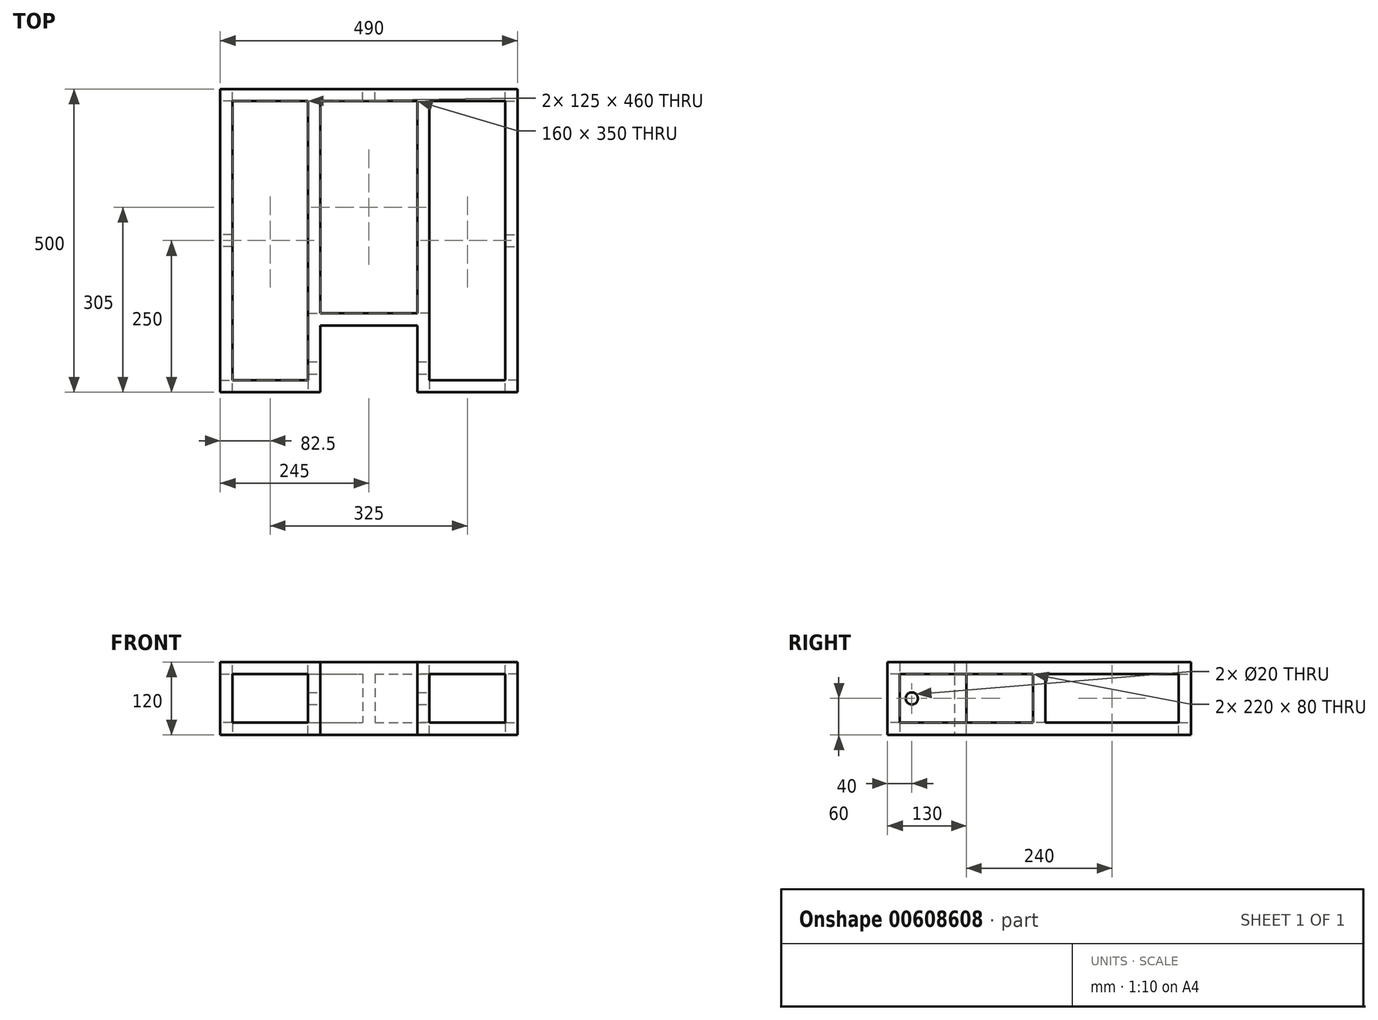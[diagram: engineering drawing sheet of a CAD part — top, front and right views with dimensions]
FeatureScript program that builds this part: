
annotation { "Feature Type Name" : "Feature", "Feature Type Description" : "" }
export const myFeature = defineFeature(function(context is Context, id is Id, definition is map)
    precondition{}
    {
        {
            var Q0;
            Q0=qCreatedBy(makeId("Front.planeOp"),FACE);
            var sketch = newSketch(context, id + "F0", { "sketchPlane" : qUnion([Q0])});
            skLineSegment(sketch, "E0.bottom", {"start": v(0, 0) * mm, "end": v(20, 0) * mm});
            skLineSegment(sketch, "E0.top", {"start": v(0, 20) * mm, "end": v(20, 20) * mm});
            skLineSegment(sketch, "E0.left", {"start": v(0, 0) * mm, "end": v(0, 20) * mm});
            skLineSegment(sketch, "E0.right", {"start": v(20, 0) * mm, "end": v(20, 20) * mm});
            skSolve(sketch);
        }
        {
            var Q0;
            Q0=makeQuery(id+"F0.imprint","IMPRINT",FACE,{"disambiguationData":[TD([[makeQuery(id+"F0.imprint","IMPRINT",EDGE,{"derivedFrom":sQuery(id+"F0.wireOp",EDGE,"E0.bottom")}),1.0]])]});
            extrude(context, id + "F1", {"entities" : qUnion([Q0]), "depth" : 500 * mm, "offsetDistance" : 25 * mm});
        }
        {
            var Q0;
            Q0=makeQuery(id+"F1.opExtrude","SWEPT_FACE",FACE,{"disambiguationData":[OSD([sQuery(id+"F0.wireOp",EDGE,"E0.left")])]});
            var sketch = newSketch(context, id + "F2", { "sketchPlane" : qUnion([Q0])});
            skLineSegment(sketch, "E1.bottom", {"start": v(0, 20) * mm, "end": v(20, 20) * mm});
            skLineSegment(sketch, "E1.top", {"start": v(0, 0) * mm, "end": v(20, 0) * mm});
            skLineSegment(sketch, "E1.left", {"start": v(0, 20) * mm, "end": v(0, 0) * mm});
            skLineSegment(sketch, "E1.right", {"start": v(20, 20) * mm, "end": v(20, 0) * mm});
            skLineSegment(sketch, "E2.bottom", {"start": v(500, 0) * mm, "end": v(480, 0) * mm});
            skLineSegment(sketch, "E2.top", {"start": v(500, 20) * mm, "end": v(480, 20) * mm});
            skLineSegment(sketch, "E2.left", {"start": v(500, 0) * mm, "end": v(500, 20) * mm});
            skLineSegment(sketch, "E2.right", {"start": v(480, 0) * mm, "end": v(480, 20) * mm});
            skSolve(sketch);
        }
        {
            var Q0;
            Q0 = qSketchRegion(id + "F2", true);
            extrude(context, id + "F3", {"entities" : qUnion([Q0]), "operationType" : NewBodyOperationType.ADD, "depth" : 470 * mm, "offsetDistance" : 25 * mm});
        }
        {
            var Q0;
            Q0=makeQuery(id+"F3.opExtrude","SWEPT_FACE",FACE,{"disambiguationData":[OSD([sQuery(id+"F2.wireOp",EDGE,"E1.right")])]});
            var sketch = newSketch(context, id + "F4", { "sketchPlane" : qUnion([Q0])});
            skLineSegment(sketch, "E3.bottom", {"start": v(-470, 20) * mm, "end": v(-450, 20) * mm});
            skLineSegment(sketch, "E3.top", {"start": v(-470, 0) * mm, "end": v(-450, 0) * mm});
            skLineSegment(sketch, "E3.left", {"start": v(-470, 20) * mm, "end": v(-470, 0) * mm});
            skLineSegment(sketch, "E3.right", {"start": v(-450, 20) * mm, "end": v(-450, 0) * mm});
            skSolve(sketch);
        }
        {
            var Q0;
            Q0=makeQuery(id+"F4.imprint","IMPRINT",FACE,{"disambiguationData":[TD([[makeQuery(id+"F4.imprint","IMPRINT",EDGE,{"derivedFrom":sQuery(id+"F4.wireOp",EDGE,"E3.bottom")}),-1.0]])]});
            extrude(context, id + "F5", {"entities" : qUnion([Q0]), "operationType" : NewBodyOperationType.ADD, "endBound" : BoundingType.UP_TO_NEXT, "depth" : 25 * mm, "offsetDistance" : 25 * mm});
        }
        {
            var Q0;
            Q0=makeQuery(id+"F3.opExtrude","SWEPT_FACE",FACE,{"disambiguationData":[OSD([sQuery(id+"F2.wireOp",EDGE,"E2.right")])]});
            var sketch = newSketch(context, id + "F6", { "sketchPlane" : qUnion([Q0])});
            skLineSegment(sketch, "E4.bottom", {"start": v(125, 20) * mm, "end": v(145, 20) * mm});
            skLineSegment(sketch, "E4.top", {"start": v(125, 0) * mm, "end": v(145, 0) * mm});
            skLineSegment(sketch, "E4.left", {"start": v(125, 20) * mm, "end": v(125, 0) * mm});
            skLineSegment(sketch, "E4.right", {"start": v(145, 20) * mm, "end": v(145, 0) * mm});
            skLineSegment(sketch, "E5.bottom", {"start": v(305, 20) * mm, "end": v(325, 20) * mm});
            skLineSegment(sketch, "E5.top", {"start": v(305, 0) * mm, "end": v(325, 0) * mm});
            skLineSegment(sketch, "E5.left", {"start": v(305, 20) * mm, "end": v(305, 0) * mm});
            skLineSegment(sketch, "E5.right", {"start": v(325, 20) * mm, "end": v(325, 0) * mm});
            skSolve(sketch);
        }
        {
            var Q0;
            Q0=makeQuery(id+"F6.imprint","IMPRINT",FACE,{"disambiguationData":[TD([[makeQuery(id+"F6.imprint","IMPRINT",EDGE,{"derivedFrom":sQuery(id+"F6.wireOp",EDGE,"E4.bottom")}),1.0]])]});
            var Q1;
            Q1=makeQuery(id+"F6.imprint","IMPRINT",FACE,{"disambiguationData":[TD([[makeQuery(id+"F6.imprint","IMPRINT",EDGE,{"derivedFrom":sQuery(id+"F6.wireOp",EDGE,"E5.bottom")}),1.0]])]});
            extrude(context, id + "F7", {"entities" : qUnion([Q0, Q1]), "operationType" : NewBodyOperationType.ADD, "depth" : 110 * mm, "offsetDistance" : 25 * mm});
        }
        {
            var Q0;
            Q0=makeQuery(id+"F7.opExtrude","SWEPT_FACE",FACE,{"disambiguationData":[OSD([sQuery(id+"F6.wireOp",EDGE,"E4.right")])]});
            var sketch = newSketch(context, id + "F8", { "sketchPlane" : qUnion([Q0])});
            skLineSegment(sketch, "E6.bottom", {"start": v(370, 20) * mm, "end": v(390, 20) * mm});
            skLineSegment(sketch, "E6.top", {"start": v(370, 0) * mm, "end": v(390, 0) * mm});
            skLineSegment(sketch, "E6.left", {"start": v(370, 20) * mm, "end": v(370, 0) * mm});
            skLineSegment(sketch, "E6.right", {"start": v(390, 20) * mm, "end": v(390, 0) * mm});
            skSolve(sketch);
        }
        {
            var Q0;
            Q0=makeQuery(id+"F8.imprint","IMPRINT",FACE,{"disambiguationData":[TD([[makeQuery(id+"F8.imprint","IMPRINT",EDGE,{"derivedFrom":sQuery(id+"F8.wireOp",EDGE,"E6.bottom")}),-1.0]])]});
            extrude(context, id + "F9", {"entities" : qUnion([Q0]), "operationType" : NewBodyOperationType.ADD, "endBound" : BoundingType.UP_TO_NEXT, "depth" : 25 * mm, "offsetDistance" : 25 * mm});
        }
        {
            var Q0;
            Q0=makeQuery(id+"F5.boolean.opBoolean","MERGE",FACE,{"derivedFrom":[makeQuery(id+"F3.boolean.opBoolean","MERGE",FACE,{"derivedFrom":[makeQuery(id+"F1.opExtrude","SWEPT_FACE",FACE,{"disambiguationData":[OSD([sQuery(id+"F0.wireOp",EDGE,"E0.top")])]}),makeQuery(id+"F3.opExtrude","SWEPT_FACE",FACE,{"disambiguationData":[OSD([sQuery(id+"F2.wireOp",EDGE,"E1.bottom")])]}),makeQuery(id+"F3.opExtrude","SWEPT_FACE",FACE,{"disambiguationData":[OSD([sQuery(id+"F2.wireOp",EDGE,"E2.top")])]})]}),makeQuery(id+"F5.opExtrude","SWEPT_FACE",FACE,{"disambiguationData":[OSD([sQuery(id+"F4.wireOp",EDGE,"E3.bottom")])]})]});
            var sketch = newSketch(context, id + "F10", { "sketchPlane" : qUnion([Q0])});
            skLineSegment(sketch, "E7.bottom", {"start": v(-470, -500) * mm, "end": v(-450, -500) * mm});
            skLineSegment(sketch, "E7.top", {"start": v(-470, -480) * mm, "end": v(-450, -480) * mm});
            skLineSegment(sketch, "E7.left", {"start": v(-470, -500) * mm, "end": v(-470, -480) * mm});
            skLineSegment(sketch, "E7.right", {"start": v(-450, -500) * mm, "end": v(-450, -480) * mm});
            skLineSegment(sketch, "E8.bottom", {"start": v(20, -500) * mm, "end": v(0, -500) * mm});
            skLineSegment(sketch, "E8.top", {"start": v(20, -480) * mm, "end": v(0, -480) * mm});
            skLineSegment(sketch, "E8.left", {"start": v(20, -500) * mm, "end": v(20, -480) * mm});
            skLineSegment(sketch, "E8.right", {"start": v(0, -500) * mm, "end": v(0, -480) * mm});
            skLineSegment(sketch, "E9.bottom", {"start": v(-450, -20) * mm, "end": v(-470, -20) * mm});
            skLineSegment(sketch, "E9.top", {"start": v(-450, 0) * mm, "end": v(-470, 0) * mm});
            skLineSegment(sketch, "E9.left", {"start": v(-450, -20) * mm, "end": v(-450, 0) * mm});
            skLineSegment(sketch, "E9.right", {"start": v(-470, -20) * mm, "end": v(-470, 0) * mm});
            skLineSegment(sketch, "E10.bottom", {"start": v(0, -20) * mm, "end": v(20, -20) * mm});
            skLineSegment(sketch, "E10.top", {"start": v(0, 0) * mm, "end": v(20, 0) * mm});
            skLineSegment(sketch, "E10.left", {"start": v(0, -20) * mm, "end": v(0, 0) * mm});
            skLineSegment(sketch, "E10.right", {"start": v(20, -20) * mm, "end": v(20, 0) * mm});
            skLineSegment(sketch, "E11.bottom", {"start": v(0, -260) * mm, "end": v(20, -260) * mm});
            skLineSegment(sketch, "E11.top", {"start": v(0, -240) * mm, "end": v(20, -240) * mm});
            skLineSegment(sketch, "E11.left", {"start": v(0, -260) * mm, "end": v(0, -240) * mm});
            skLineSegment(sketch, "E11.right", {"start": v(20, -260) * mm, "end": v(20, -240) * mm});
            skLineSegment(sketch, "E12.bottom", {"start": v(-450, -260) * mm, "end": v(-470, -260) * mm});
            skLineSegment(sketch, "E12.top", {"start": v(-450, -240) * mm, "end": v(-470, -240) * mm});
            skLineSegment(sketch, "E12.left", {"start": v(-450, -260) * mm, "end": v(-450, -240) * mm});
            skLineSegment(sketch, "E12.right", {"start": v(-470, -260) * mm, "end": v(-470, -240) * mm});
            skLineSegment(sketch, "E13.bottom", {"start": v(-325, -370) * mm, "end": v(-305, -370) * mm});
            skLineSegment(sketch, "E13.top", {"start": v(-325, -500) * mm, "end": v(-305, -500) * mm});
            skLineSegment(sketch, "E13.left", {"start": v(-325, -370) * mm, "end": v(-325, -500) * mm});
            skLineSegment(sketch, "E13.right", {"start": v(-305, -370) * mm, "end": v(-305, -500) * mm});
            skLineSegment(sketch, "E14.bottom", {"start": v(-125, -370) * mm, "end": v(-145, -370) * mm});
            skLineSegment(sketch, "E14.top", {"start": v(-125, -500) * mm, "end": v(-145, -500) * mm});
            skLineSegment(sketch, "E14.left", {"start": v(-125, -370) * mm, "end": v(-125, -500) * mm});
            skLineSegment(sketch, "E14.right", {"start": v(-145, -370) * mm, "end": v(-145, -500) * mm});
            skLineSegment(sketch, "E15.bottom", {"start": v(-235, -20) * mm, "end": v(-215, -20) * mm});
            skLineSegment(sketch, "E15.top", {"start": v(-235, 0) * mm, "end": v(-215, 0) * mm});
            skLineSegment(sketch, "E15.left", {"start": v(-235, -20) * mm, "end": v(-235, 0) * mm});
            skLineSegment(sketch, "E15.right", {"start": v(-215, -20) * mm, "end": v(-215, 0) * mm});
            skSolve(sketch);
        }
        {
            var Q0;
            Q0 = qSketchRegion(id + "F10", true);
            extrude(context, id + "F11", {"entities" : qUnion([Q0]), "operationType" : NewBodyOperationType.ADD, "depth" : 40 * mm, "offsetDistance" : 25 * mm});
        }
        {
            var Q0;
            Q0=makeQuery(id+"F1.opExtrude","SWEPT_BODY",BODY,{"disambiguationData":[OSD([sQuery(id+"F0.wireOp",EDGE,"E0.bottom"),sQuery(id+"F0.wireOp",EDGE,"E0.top"),sQuery(id+"F0.wireOp",EDGE,"E0.left"),sQuery(id+"F0.wireOp",EDGE,"E0.right")])]});
            var Q1;
            Q1=makeQuery(id+"F11.opExtrude","CAP_FACE",FACE,{"disambiguationData":[OSD([sQuery(id+"F10.wireOp",EDGE,"E10.bottom"),sQuery(id+"F10.wireOp",EDGE,"E10.top"),sQuery(id+"F10.wireOp",EDGE,"E10.left"),sQuery(id+"F10.wireOp",EDGE,"E10.right")])],"isStart":false});
            mirror(context, id + "F12", {"operationType" : NewBodyOperationType.ADD, "entities" : qUnion([Q0]), "mirrorPlane" : qUnion([Q1])});
        }
        {
            var Q0;
            Q0=makeQuery(id+"F12.opPattern","COPY",FACE,{"derivedFrom":makeQuery(id+"F9.boolean.opBoolean","MERGE",FACE,{"derivedFrom":[makeQuery(id+"F7.boolean.opBoolean","MERGE",FACE,{"derivedFrom":[makeQuery(id+"F5.boolean.opBoolean","MERGE",FACE,{"derivedFrom":[makeQuery(id+"F3.boolean.opBoolean","MERGE",FACE,{"derivedFrom":[makeQuery(id+"F1.opExtrude","SWEPT_FACE",FACE,{"disambiguationData":[OSD([sQuery(id+"F0.wireOp",EDGE,"E0.bottom")])]}),makeQuery(id+"F3.opExtrude","SWEPT_FACE",FACE,{"disambiguationData":[OSD([sQuery(id+"F2.wireOp",EDGE,"E1.top")])]}),makeQuery(id+"F3.opExtrude","SWEPT_FACE",FACE,{"disambiguationData":[OSD([sQuery(id+"F2.wireOp",EDGE,"E2.bottom")])]})]}),makeQuery(id+"F5.opExtrude","SWEPT_FACE",FACE,{"disambiguationData":[OSD([sQuery(id+"F4.wireOp",EDGE,"E3.top")])]})]}),makeQuery(id+"F7.opExtrude","SWEPT_FACE",FACE,{"disambiguationData":[OSD([sQuery(id+"F6.wireOp",EDGE,"E4.top")])]}),makeQuery(id+"F7.opExtrude","SWEPT_FACE",FACE,{"disambiguationData":[OSD([sQuery(id+"F6.wireOp",EDGE,"E5.top")])]})]}),makeQuery(id+"F9.opExtrude","SWEPT_FACE",FACE,{"disambiguationData":[OSD([sQuery(id+"F8.wireOp",EDGE,"E6.top")])]})]}),"instanceName":"1"});
            var sketch = newSketch(context, id + "F13", { "sketchPlane" : qUnion([Q0])});
            skLineSegment(sketch, "E16.bottom", {"start": v(-305, -480) * mm, "end": v(-145, -480) * mm});
            skLineSegment(sketch, "E16.top", {"start": v(-305, -500) * mm, "end": v(-145, -500) * mm});
            skLineSegment(sketch, "E16.left", {"start": v(-305, -480) * mm, "end": v(-305, -500) * mm});
            skLineSegment(sketch, "E16.right", {"start": v(-145, -480) * mm, "end": v(-145, -500) * mm});
            skSolve(sketch);
        }
        {
            var Q0;
            Q0 = qSketchRegion(id + "F13", true);
            extrude(context, id + "F14", {"entities" : qUnion([Q0]), "operationType" : NewBodyOperationType.REMOVE, "endBound" : BoundingType.THROUGH_ALL, "oppositeDirection" : true, "depth" : 25 * mm, "offsetDistance" : 25 * mm});
        }
        {
            var Q0;
            {var subQ0=makeQuery(id+"F11.boolean.opBoolean","MERGE",FACE,{"derivedFrom":[makeQuery(id+"F7.opExtrude","SWEPT_FACE",FACE,{"disambiguationData":[OSD([sQuery(id+"F6.wireOp",EDGE,"E4.left")])]}),makeQuery(id+"F11.opExtrude","SWEPT_FACE",FACE,{"disambiguationData":[OSD([sQuery(id+"F10.wireOp",EDGE,"E14.left")])]})]});Q0=makeQuery(id+"F12.boolean.opBoolean","MERGE",FACE,{"derivedFrom":[subQ0,makeQuery(id+"F12.opPattern","COPY",FACE,{"derivedFrom":subQ0,"instanceName":"1"})]});}
            var sketch = newSketch(context, id + "F15", { "sketchPlane" : qUnion([Q0])});
            skPoint(sketch, "E17", {"position": v(-460, 60) * mm});
            skSolve(sketch);
        }
        {
            var Q0;
            Q0=sQuery(id+"F15.wireOp",VERTEX,"E17");
            var Q1;
            Q1=makeQuery(id+"F1.opExtrude","SWEPT_BODY",BODY,{"disambiguationData":[OSD([sQuery(id+"F0.wireOp",EDGE,"E0.bottom"),sQuery(id+"F0.wireOp",EDGE,"E0.top"),sQuery(id+"F0.wireOp",EDGE,"E0.left"),sQuery(id+"F0.wireOp",EDGE,"E0.right")])]});
            hole(context, id + "F16", {"style" : HoleStyle.SIMPLE, "endStyle" : HoleEndStyle.BLIND, "holeDiameter" : 20 * mm, "majorDiameter" : 5 * mm, "holeDepth" : 250 * mm, "isTappedThrough" : true, "tappedDepth" : 12 * mm, "tapClearance" : 3, "locations" : qUnion([Q0]), "scope" : qUnion([Q1])});
        }
        {
            var Q0;
            {var subQ0=makeQuery(id+"F11.boolean.opBoolean","MERGE",FACE,{"derivedFrom":[makeQuery(id+"F9.boolean.opBoolean","MERGE",FACE,{"derivedFrom":[makeQuery(id+"F7.opExtrude","CAP_FACE",FACE,{"disambiguationData":[OSD([sQuery(id+"F6.wireOp",EDGE,"E4.bottom"),sQuery(id+"F6.wireOp",EDGE,"E4.top"),sQuery(id+"F6.wireOp",EDGE,"E4.left"),sQuery(id+"F6.wireOp",EDGE,"E4.right")])],"isStart":false}),makeQuery(id+"F7.opExtrude","CAP_FACE",FACE,{"disambiguationData":[OSD([sQuery(id+"F6.wireOp",EDGE,"E5.bottom"),sQuery(id+"F6.wireOp",EDGE,"E5.top"),sQuery(id+"F6.wireOp",EDGE,"E5.left"),sQuery(id+"F6.wireOp",EDGE,"E5.right")])],"isStart":false}),makeQuery(id+"F9.opExtrude","SWEPT_FACE",FACE,{"disambiguationData":[OSD([sQuery(id+"F8.wireOp",EDGE,"E6.left")])]})]}),makeQuery(id+"F11.opExtrude","SWEPT_FACE",FACE,{"disambiguationData":[OSD([sQuery(id+"F10.wireOp",EDGE,"E13.bottom")])]}),makeQuery(id+"F11.opExtrude","SWEPT_FACE",FACE,{"disambiguationData":[OSD([sQuery(id+"F10.wireOp",EDGE,"E14.bottom")])]})]});Q0=makeQuery(id+"F12.boolean.opBoolean","MERGE",FACE,{"derivedFrom":[subQ0,makeQuery(id+"F12.opPattern","COPY",FACE,{"derivedFrom":subQ0,"instanceName":"1"})]});}
            var sketch = newSketch(context, id + "F17", { "sketchPlane" : qUnion([Q0])});
            skLineSegment(sketch, "E18.bottom", {"start": v(145, 20) * mm, "end": v(305, 20) * mm});
            skLineSegment(sketch, "E18.top", {"start": v(145, 100) * mm, "end": v(305, 100) * mm});
            skLineSegment(sketch, "E18.left", {"start": v(145, 20) * mm, "end": v(145, 100) * mm});
            skLineSegment(sketch, "E18.right", {"start": v(305, 20) * mm, "end": v(305, 100) * mm});
            skSolve(sketch);
        }
        {
            var Q0;
            Q0=makeQuery(id+"F17.imprint","IMPRINT",FACE,{"disambiguationData":[TD([[makeQuery(id+"F17.imprint","IMPRINT",EDGE,{"derivedFrom":sQuery(id+"F17.wireOp",EDGE,"E18.bottom")}),-1.0]])]});
            extrude(context, id + "F18", {"entities" : qUnion([Q0]), "operationType" : NewBodyOperationType.ADD, "oppositeDirection" : true, "depth" : 20 * mm, "offsetDistance" : 25 * mm});
        }
        {
            var Q0;
            {var subQ0=makeQuery(id+"F11.boolean.opBoolean","MERGE",FACE,{"derivedFrom":[makeQuery(id+"F9.boolean.opBoolean","MERGE",FACE,{"derivedFrom":[makeQuery(id+"F7.opExtrude","CAP_FACE",FACE,{"disambiguationData":[OSD([sQuery(id+"F6.wireOp",EDGE,"E4.bottom"),sQuery(id+"F6.wireOp",EDGE,"E4.top"),sQuery(id+"F6.wireOp",EDGE,"E4.left"),sQuery(id+"F6.wireOp",EDGE,"E4.right")])],"isStart":false}),makeQuery(id+"F7.opExtrude","CAP_FACE",FACE,{"disambiguationData":[OSD([sQuery(id+"F6.wireOp",EDGE,"E5.bottom"),sQuery(id+"F6.wireOp",EDGE,"E5.top"),sQuery(id+"F6.wireOp",EDGE,"E5.left"),sQuery(id+"F6.wireOp",EDGE,"E5.right")])],"isStart":false}),makeQuery(id+"F9.opExtrude","SWEPT_FACE",FACE,{"disambiguationData":[OSD([sQuery(id+"F8.wireOp",EDGE,"E6.left")])]})]}),makeQuery(id+"F11.opExtrude","SWEPT_FACE",FACE,{"disambiguationData":[OSD([sQuery(id+"F10.wireOp",EDGE,"E13.bottom")])]}),makeQuery(id+"F11.opExtrude","SWEPT_FACE",FACE,{"disambiguationData":[OSD([sQuery(id+"F10.wireOp",EDGE,"E14.bottom")])]})]});Q0=makeQuery(id+"F18.boolean.opBoolean","MERGE",FACE,{"derivedFrom":[makeQuery(id+"F12.boolean.opBoolean","MERGE",FACE,{"derivedFrom":[subQ0,makeQuery(id+"F12.opPattern","COPY",FACE,{"derivedFrom":subQ0,"instanceName":"1"})]}),makeQuery(id+"F18.opExtrude","CAP_FACE",FACE,{"disambiguationData":[OSD([sQuery(id+"F17.wireOp",EDGE,"E18.bottom"),sQuery(id+"F17.wireOp",EDGE,"E18.top"),sQuery(id+"F17.wireOp",EDGE,"E18.left"),sQuery(id+"F17.wireOp",EDGE,"E18.right")])],"isStart":true})]});}
            var sketch = newSketch(context, id + "F19", { "sketchPlane" : qUnion([Q0])});
            skLineSegment(sketch, "E19.bottom", {"start": v(125, 120) * mm, "end": v(145, 120) * mm});
            skLineSegment(sketch, "E19.top", {"start": v(125, 100) * mm, "end": v(145, 100) * mm});
            skLineSegment(sketch, "E19.left", {"start": v(125, 120) * mm, "end": v(125, 100) * mm});
            skLineSegment(sketch, "E19.right", {"start": v(145, 120) * mm, "end": v(145, 100) * mm});
            skLineSegment(sketch, "E20.bottom", {"start": v(125, 0) * mm, "end": v(145, 0) * mm});
            skLineSegment(sketch, "E20.top", {"start": v(125, 20) * mm, "end": v(145, 20) * mm});
            skLineSegment(sketch, "E20.left", {"start": v(125, 0) * mm, "end": v(125, 20) * mm});
            skLineSegment(sketch, "E20.right", {"start": v(145, 0) * mm, "end": v(145, 20) * mm});
            skLineSegment(sketch, "E21.bottom", {"start": v(325, 120) * mm, "end": v(305, 120) * mm});
            skLineSegment(sketch, "E21.top", {"start": v(325, 100) * mm, "end": v(305, 100) * mm});
            skLineSegment(sketch, "E21.left", {"start": v(325, 120) * mm, "end": v(325, 100) * mm});
            skLineSegment(sketch, "E21.right", {"start": v(305, 120) * mm, "end": v(305, 100) * mm});
            skLineSegment(sketch, "E22.bottom", {"start": v(325, 0) * mm, "end": v(305, 0) * mm});
            skLineSegment(sketch, "E22.top", {"start": v(325, 20) * mm, "end": v(305, 20) * mm});
            skLineSegment(sketch, "E22.left", {"start": v(325, 0) * mm, "end": v(325, 20) * mm});
            skLineSegment(sketch, "E22.right", {"start": v(305, 0) * mm, "end": v(305, 20) * mm});
            skSolve(sketch);
        }
        {
            var Q0;
            Q0=makeQuery(id+"F19.imprint","IMPRINT",FACE,{"disambiguationData":[TD([[makeQuery(id+"F19.imprint","IMPRINT",EDGE,{"derivedFrom":sQuery(id+"F19.wireOp",EDGE,"E20.bottom")}),-1.0]])]});
            var Q1;
            Q1=makeQuery(id+"F19.imprint","IMPRINT",FACE,{"disambiguationData":[TD([[makeQuery(id+"F19.imprint","IMPRINT",EDGE,{"derivedFrom":sQuery(id+"F19.wireOp",EDGE,"E22.bottom")}),-1.0]])]});
            var Q2;
            Q2=makeQuery(id+"F19.imprint","IMPRINT",FACE,{"disambiguationData":[TD([[makeQuery(id+"F19.imprint","IMPRINT",EDGE,{"derivedFrom":sQuery(id+"F19.wireOp",EDGE,"E21.bottom")}),1.0]])]});
            var Q3;
            Q3=makeQuery(id+"F19.imprint","IMPRINT",FACE,{"disambiguationData":[TD([[makeQuery(id+"F19.imprint","IMPRINT",EDGE,{"derivedFrom":sQuery(id+"F19.wireOp",EDGE,"E19.bottom")}),1.0]])]});
            extrude(context, id + "F20", {"entities" : qUnion([Q0, Q1, Q2, Q3]), "operationType" : NewBodyOperationType.ADD, "endBound" : BoundingType.UP_TO_NEXT, "depth" : 25 * mm, "offsetDistance" : 25 * mm});
        }
    });
